# Revit family: RBA8889
name_source: partatom
category: Plumbing Fixtures
revit_build: Autodesk Revit MEP 2012 (Build: 20110309_2315)
units: mm (PartAtom-declared; Revit-internal decimal feet)

## types (8) — shared parameters
Basin = Satin Stainless Steel
Basin 1 = Yes
Manufacturer = RBA
Tap = Satin Stainless Steel
URL = www.rba.com.au/basins/basins

## per-type parameters (varying)
| type | Backsplash Length | Basin 2 | Basin 3 | Basin 4 | Counter 2 | Counter 3 | Counter 4 | Cover 1 | Cover 2 | Cover 3 | Cover 4 | Description |
| RBA8889-181 | 483 mm | No | No | No | No | No | No | No | No | No | No | Curvalinear Single Basin |
| RBA8889-282 | 1245 mm | Yes | No | No | Yes | No | No | Yes | Yes | No | No | Curvalinear Double Basin With Trap Cover |
| RBA8889-382 | 2005 mm  [stored 6.57808 ft] | Yes | Yes | No | Yes | Yes | No | Yes | Yes | Yes | No | Curvalinear Triple Basin With Trap Cover |
| RBA8889-482 | 2770 mm  [stored 9.08793 ft] | Yes | Yes | Yes | Yes | Yes | Yes | Yes | Yes | Yes | Yes | Curvalinear Quad Basin With Trap Cover |
| RBA8889-182 | 483 mm | No | No | No | No | No | No | Yes | No | No | No | Curvalinear Single Basin With Trap Cover |
| RBA8889-281 | 1245 mm | Yes | No | No | Yes | No | No | No | No | No | No | Curvalinear Double Basin |
| RBA8889-381 | 2005 mm  [stored 6.57808 ft] | Yes | Yes | No | Yes | Yes | No | No | No | No | No | Curvalinear Triple Basin |
| RBA8889-481 | 2770 mm  [stored 9.08793 ft] | Yes | Yes | Yes | Yes | Yes | Yes | No | No | No | No | Curvalinear Quad Basin |

note: column(s) folded — value = type name in every type: Model

note: [stored X ft] marks values corroborated as IEEE doubles in the binary element streams (Revit-internal decimal feet)

## geometry (parser evidence)
native form markers: Blend x2, Sweep x5
no freeform markers — native parametric forms only
